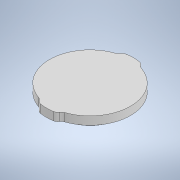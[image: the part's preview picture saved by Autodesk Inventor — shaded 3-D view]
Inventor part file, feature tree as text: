
AUTODESK INVENTOR PART (.ipt)
format: ipt  version: 2022 (Build 260153000, 153)  size: 163,840 bytes
history: native  units: in
note: dims shown in document units (in); Inventor stores cm internally (conversion verified against a paired STEP export)
features: sketch x4, extrude x3, fillet x2, pattern_circular x1, revolve x1
ambient origin geometry x8: Origin, YZ Plane, XZ Plane, XY Plane, X Axis, Y Axis, Z Axis, Center Point
bodies: Solid1 (feature_tree)
feature tree (11):
  extrude  "Extrusion1"  Depth=0.1181in TaperAngle=0.0deg
  extrude  "Extrusion2"  Depth=0.2283in TaperAngle=0.0deg
  extrude  "Extrusion4"  Depth=0.3937in
  fillet  "Fillet2"  Radius=0.6299in
  pattern_circular  "Circular Pattern1"  [2 undecoded]
  revolve  "Revolution1"  [1 undecoded]
  fillet  "Fillet3"  [1 undecoded]
  sketch  "Sketch1"  dims[d0=1.9469in d1=0.1181in d2=0.0in]
  sketch  "Sketch2"  dims[d3=2.2677in d4=0.2283in d5=0.0in]
  sketch  "Sketch5"  dims[d28=0.3937in d29=0.0in d30=0.1575in d33=0.6299in]
  sketch  "Sketch6"  dims[d34=1.0892in d35=1.0892in d36=0.1181in d37=120.0deg d38=0.1181in d39=60.0deg d40=1.1339in d41=0.7874in d42=360.0deg d44=0.1604in d45=0.0787in d46=0.0394in d47=0.086in d48=0.086in d49=0.0197in]
note: 4 required parameter values undecoded (feature->parameter linkage not recoverable at this tier; creation-order binding heuristic only, values carry confidence <= 0.55)